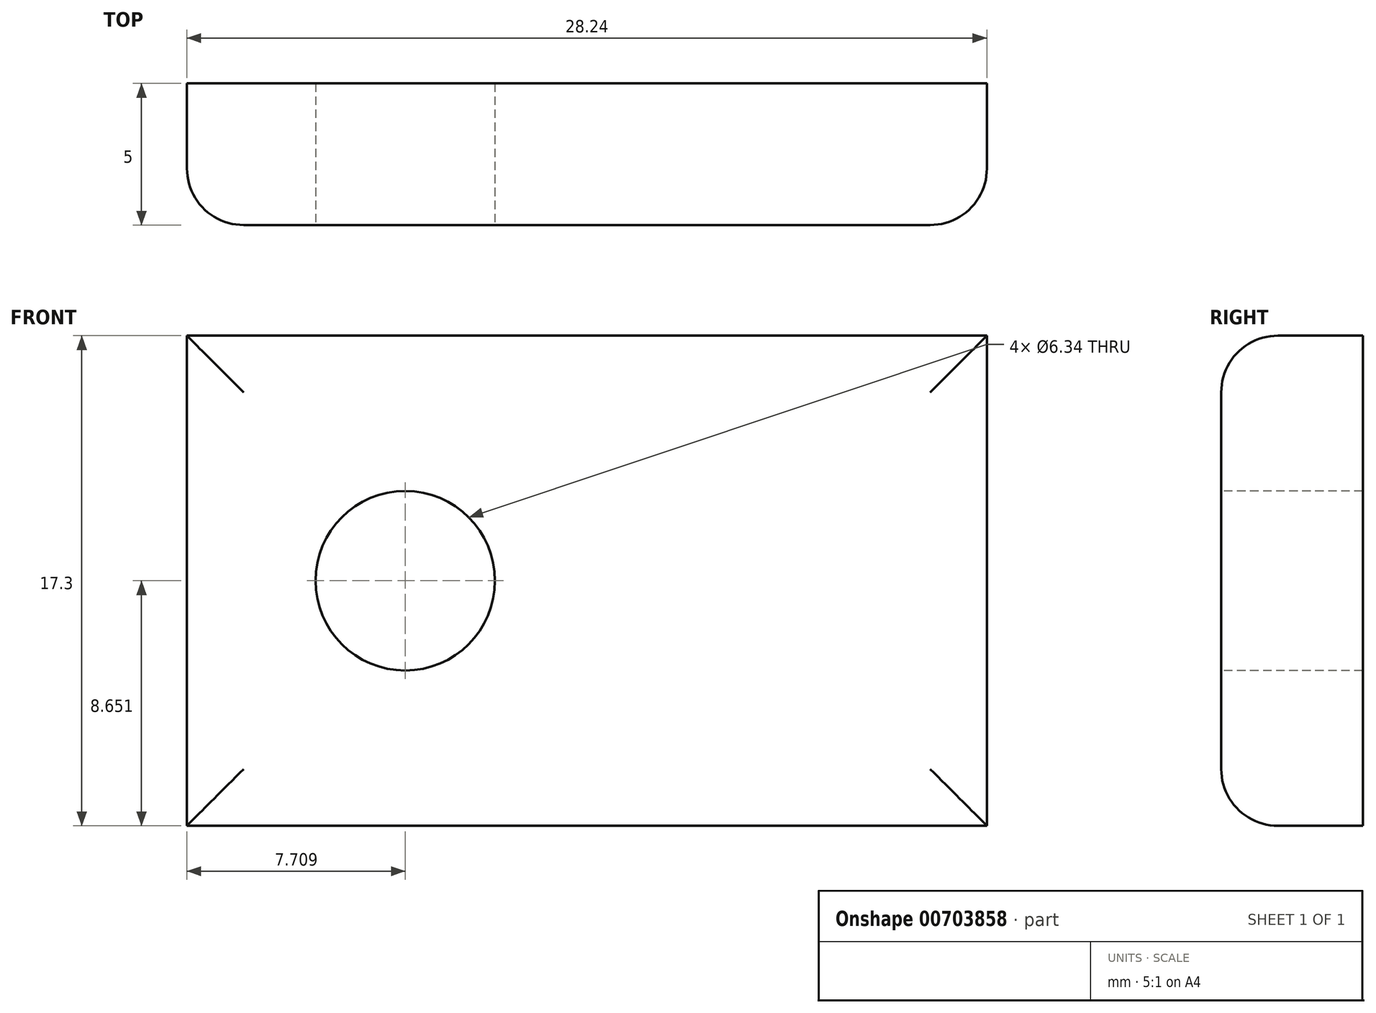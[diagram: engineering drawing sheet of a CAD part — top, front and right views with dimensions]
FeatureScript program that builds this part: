
annotation { "Feature Type Name" : "Feature", "Feature Type Description" : "" }
export const myFeature = defineFeature(function(context is Context, id is Id, definition is map)
    precondition{}
    {
        {
            var Q0;
            Q0=qCreatedBy(makeId("Front.planeOp"),FACE);
            var sketch = newSketch(context, id + "F0", { "sketchPlane" : qUnion([Q0])});
            skLineSegment(sketch, "E0.bottom", {"start": v(0, 0) * mm, "end": v(28.24, 0) * mm});
            skLineSegment(sketch, "E0.top", {"start": v(0, -17.3) * mm, "end": v(28.24, -17.3) * mm});
            skLineSegment(sketch, "E0.left", {"start": v(0, 0) * mm, "end": v(0, -17.3) * mm});
            skLineSegment(sketch, "E0.right", {"start": v(28.24, 0) * mm, "end": v(28.24, -17.3) * mm});
            skSolve(sketch);
        }
        {
            var Q0;
            Q0 = qSketchRegion(id + "F0", true);
            extrude(context, id + "F1", {"entities" : qUnion([Q0]), "depth" : 5 * mm, "offsetDistance" : 25 * mm});
        }
        {
            var Q0;
            Q0=makeQuery(id+"F1.opExtrude","CAP_EDGE",EDGE,{"disambiguationData":[OSD([sQuery(id+"F0.wireOp",EDGE,"E0.top")])],"isStart":false});
            var Q1;
            Q1=makeQuery(id+"F1.opExtrude","CAP_EDGE",EDGE,{"disambiguationData":[OSD([sQuery(id+"F0.wireOp",EDGE,"E0.right")])],"isStart":false});
            var Q2;
            Q2=makeQuery(id+"F1.opExtrude","CAP_EDGE",EDGE,{"disambiguationData":[OSD([sQuery(id+"F0.wireOp",EDGE,"E0.bottom")])],"isStart":false});
            var Q3;
            Q3=makeQuery(id+"F1.opExtrude","CAP_EDGE",EDGE,{"disambiguationData":[OSD([sQuery(id+"F0.wireOp",EDGE,"E0.left")])],"isStart":false});
            fillet(context, id + "F2", {"entities" : qUnion([Q0, Q1, Q2, Q3]), "radius" : 2 * mm, "tangentPropagation" : true, "allowEdgeOverflow" : false});
        }
        {
            var Q0;
            Q0=makeQuery(id+"F1.opExtrude","CAP_FACE",FACE,{"disambiguationData":[OSD([sQuery(id+"F0.wireOp",EDGE,"E0.bottom"),sQuery(id+"F0.wireOp",EDGE,"E0.top"),sQuery(id+"F0.wireOp",EDGE,"E0.left"),sQuery(id+"F0.wireOp",EDGE,"E0.right")])],"isStart":false});
            var sketch = newSketch(context, id + "F3", { "sketchPlane" : qUnion([Q0])});
            skCircle(sketch, "E1", {"center": v(7.7, -8.65) * mm, "radius": 3.17 * mm});
            skPoint(sketch, "E1.centerSnap0", {"position": v(2, -8.65) * mm});
            skSolve(sketch);
        }
        {
            var Q0;
            Q0 = qSketchRegion(id + "F3", true);
            extrude(context, id + "F4", {"entities" : qUnion([Q0]), "operationType" : NewBodyOperationType.REMOVE, "oppositeDirection" : true, "depth" : 25 * mm, "offsetDistance" : 25 * mm});
        }
    });
